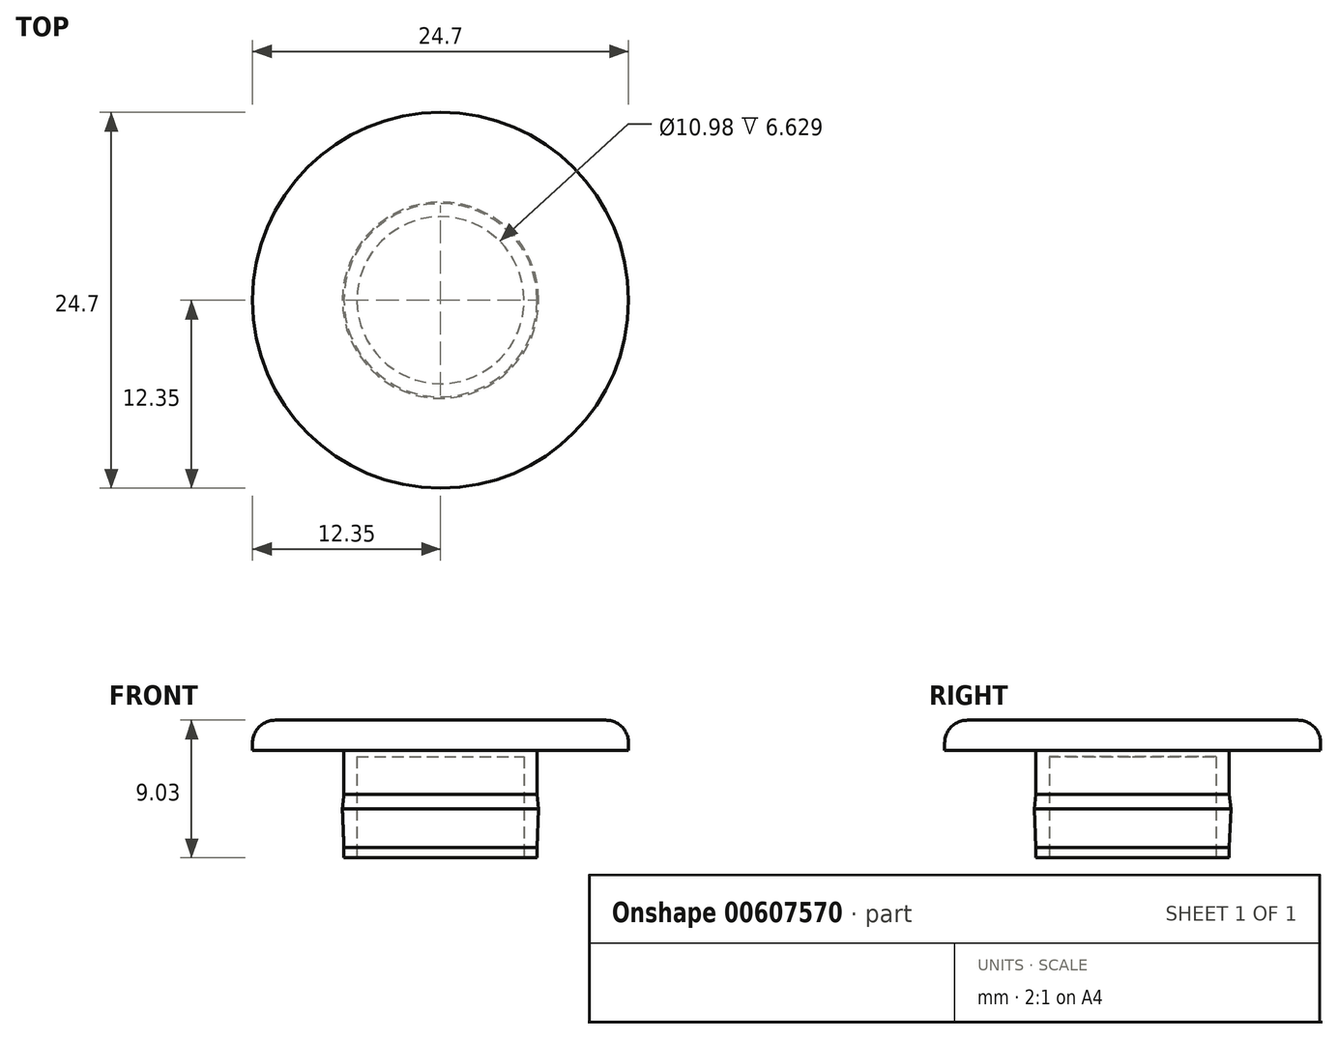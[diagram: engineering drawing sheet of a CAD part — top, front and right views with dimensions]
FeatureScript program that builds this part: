
annotation { "Feature Type Name" : "Feature", "Feature Type Description" : "" }
export const myFeature = defineFeature(function(context is Context, id is Id, definition is map)
    precondition{}
    {
        {
            var Q0;
            Q0=qCreatedBy(makeId("Right.planeOp"),FACE);
            var sketch = newSketch(context, id + "F0", { "sketchPlane" : qUnion([Q0])});
            skLineSegment(sketch, "E0", {"start": v(0, 0) * mm, "end": v(0, 32.22) * mm, "construction": true});
            skLineSegment(sketch, "E1", {"start": v(-5.49, -10.47) * mm, "end": v(-6.35, -10.47) * mm});
            skLineSegment(sketch, "E2", {"start": v(-6.35, -10.47) * mm, "end": v(-6.35, -3.44) * mm});
            skLineSegment(sketch, "E3", {"start": v(-6.35, -3.44) * mm, "end": v(-12.35, -3.44) * mm});
            skLineSegment(sketch, "E4", {"start": v(-12.35, -3.44) * mm, "end": v(-12.35, -2.94) * mm});
            skLineSegment(sketch, "E5", {"start": v(-10.85, -1.44) * mm, "end": v(0, -1.44) * mm});
            skPoint(sketch, "E6.visualSharp", {"position": v(-12.35, -1.44) * mm});
            skArc(sketch, "E6.filletArc", {"start": v(-10.85, -1.44) * mm, "mid": v(-11.91, -1.88) * mm, "end": v(-12.35, -2.94) * mm});
            skLineSegment(sketch, "E7", {"start": v(-5.49, -10.47) * mm, "end": v(-5.49, -3.84) * mm});
            skLineSegment(sketch, "E8", {"start": v(-5.49, -3.84) * mm, "end": v(0, -3.84) * mm});
            skLineSegment(sketch, "E9", {"start": v(0, -3.84) * mm, "end": v(0, -1.44) * mm});
            skPoint(sketch, "E10.orphan", {"position": v(0, -10.47) * mm});
            skLineSegment(sketch, "E11", {"start": v(-6.35, -9.82) * mm, "end": v(-6.45, -7.27) * mm});
            skLineSegment(sketch, "E12", {"start": v(-6.45, -7.27) * mm, "end": v(-6.35, -6.32) * mm});
            skSolve(sketch);
        }
        {
            var Q0;
            Q0 = qSketchRegion(id + "F0", true);
            var Q1;
            Q1=sQuery(id+"F0.wireOp",EDGE,"E0");
            revolve(context, id + "F1", {"entities" : qUnion([Q0]), "axis" : qUnion([Q1]), "revolveType" : RevolveType.FULL});
        }
    });
